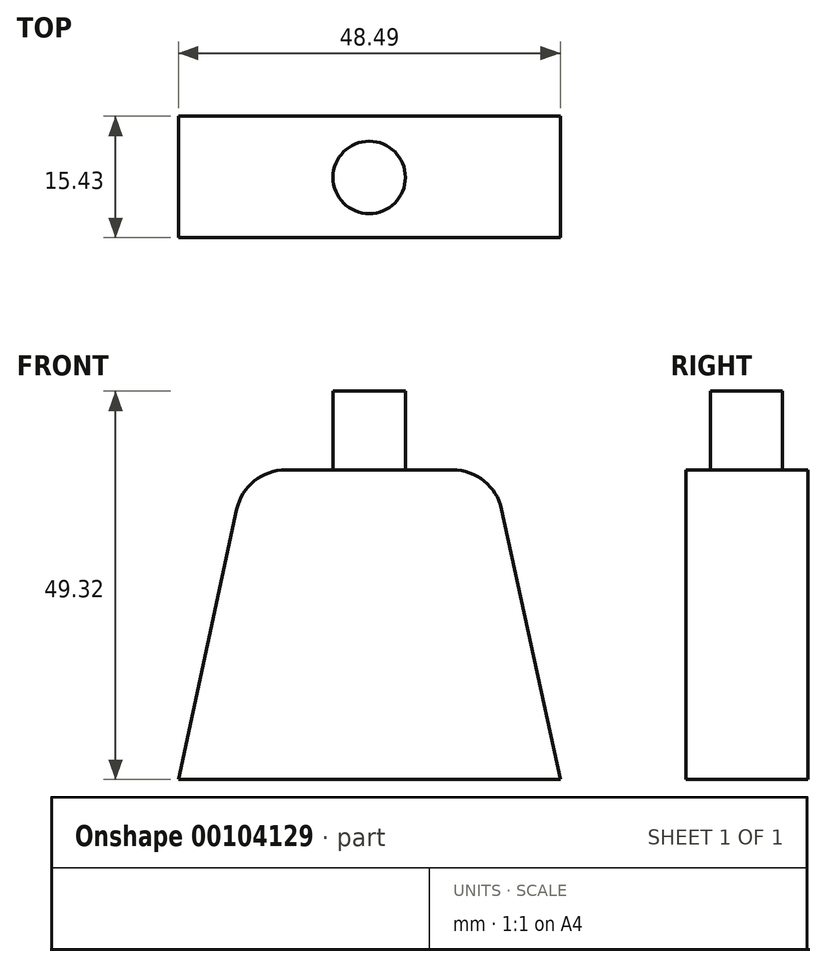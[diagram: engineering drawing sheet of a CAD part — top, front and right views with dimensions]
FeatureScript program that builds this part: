
annotation { "Feature Type Name" : "Feature", "Feature Type Description" : "" }
export const myFeature = defineFeature(function(context is Context, id is Id, definition is map)
    precondition{}
    {
        {
            var Q0;
            Q0=qCreatedBy(makeId("Front.planeOp"),FACE);
            var sketch = newSketch(context, id + "F0", { "sketchPlane" : qUnion([Q0])});
            skLineSegment(sketch, "E0", {"start": v(0, 0) * mm, "end": v(48.5, 0) * mm});
            skLineSegment(sketch, "E1", {"start": v(48.5, 0) * mm, "end": v(41.04, 34.3) * mm});
            skLineSegment(sketch, "E2", {"start": v(34.84, 39.3) * mm, "end": v(13.61, 39.3) * mm});
            skLineSegment(sketch, "E3", {"start": v(7.4, 34.3) * mm, "end": v(0, 0) * mm});
            skPoint(sketch, "E4.visualSharp", {"position": v(8.49, 39.3) * mm});
            skArc(sketch, "E4.filletArc", {"start": v(13.61, 39.3) * mm, "mid": v(9.62, 37.9) * mm, "end": v(7.4, 34.3) * mm});
            skPoint(sketch, "E5.visualSharp", {"position": v(39.96, 39.3) * mm});
            skArc(sketch, "E5.filletArc", {"start": v(41.04, 34.3) * mm, "mid": v(38.82, 37.9) * mm, "end": v(34.84, 39.3) * mm});
            skSolve(sketch);
        }
        {
            var Q0;
            Q0=makeQuery(id+"F0.imprint","IMPRINT",FACE,{"disambiguationData":[TD([[makeQuery(id+"F0.imprint","IMPRINT",EDGE,{"derivedFrom":sQuery(id+"F0.wireOp",EDGE,"E0")}),1.0]])]});
            extrude(context, id + "F1", {"entities" : qUnion([Q0]), "depth" : 15.43 * mm});
        }
        {
            var Q0;
            Q0=makeQuery(id+"F1.opExtrude","SWEPT_FACE",FACE,{"disambiguationData":[OSD([sQuery(id+"F0.wireOp",EDGE,"E2")])]});
            var sketch = newSketch(context, id + "F2", { "sketchPlane" : qUnion([Q0])});
            skCircle(sketch, "E6", {"center": v(24.22, -7.78) * mm, "radius": 4.6 * mm});
            skPoint(sketch, "E6.centerSnap0", {"position": v(24.22, -15.43) * mm});
            skSolve(sketch);
        }
        {
            var Q0;
            Q0=makeQuery(id+"F2.imprint","IMPRINT",FACE,{"disambiguationData":[TD([[makeQuery(id+"F2.imprint","IMPRINT",EDGE,{"derivedFrom":sQuery(id+"F2.wireOp",EDGE,"E6")}),1.0]])]});
            extrude(context, id + "F3", {"entities" : qUnion([Q0]), "operationType" : NewBodyOperationType.ADD, "depth" : 10.02 * mm});
        }
    });
